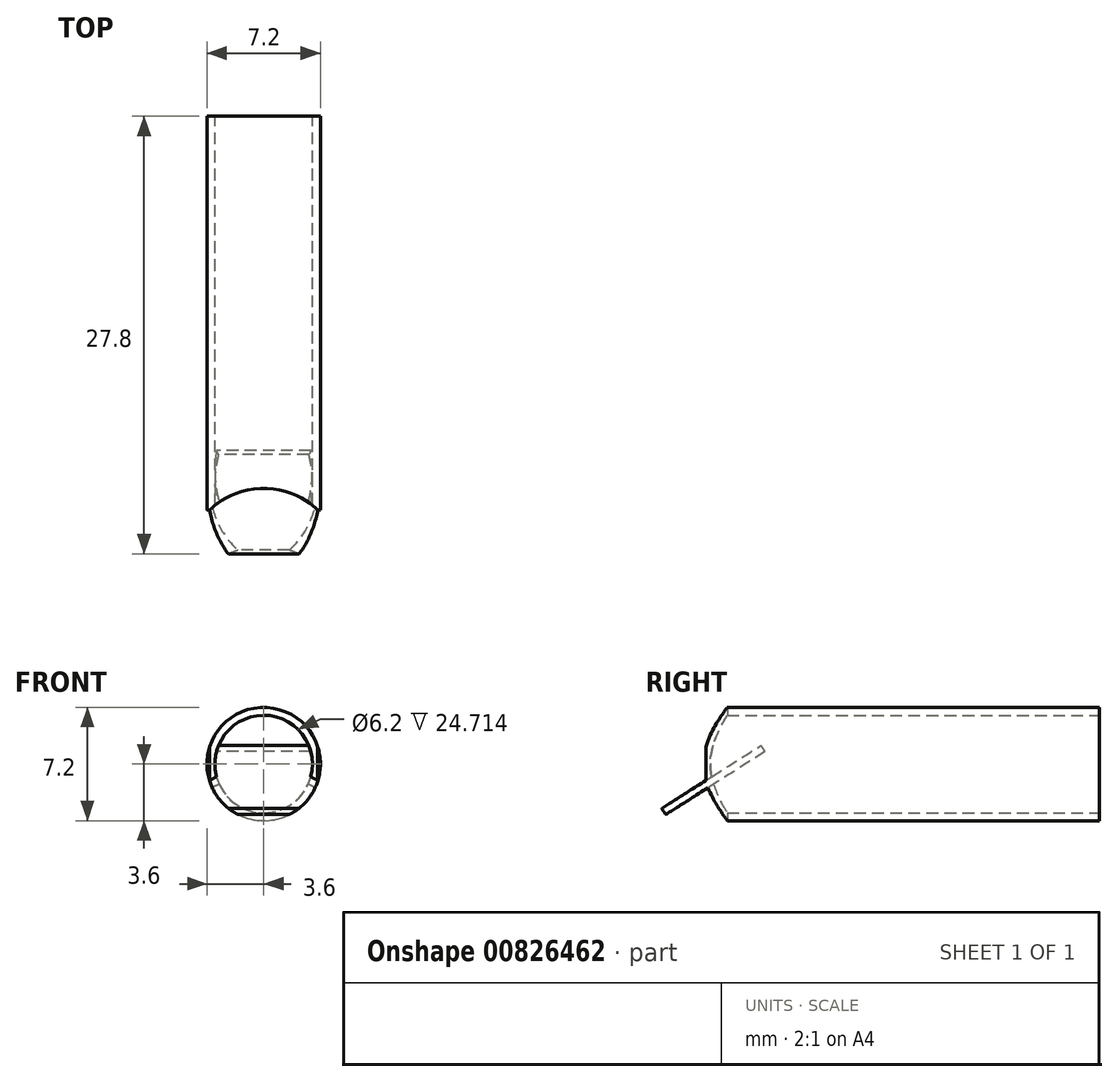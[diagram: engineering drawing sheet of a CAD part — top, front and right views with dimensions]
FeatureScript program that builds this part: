
annotation { "Feature Type Name" : "Feature", "Feature Type Description" : "" }
export const myFeature = defineFeature(function(context is Context, id is Id, definition is map)
    precondition{}
    {
        {
            var Q0;
            Q0=qCreatedBy(makeId("Front.planeOp"),FACE);
            var sketch = newSketch(context, id + "F0", { "sketchPlane" : qUnion([Q0])});
            skCircle(sketch, "E0", {"center": v(0, 0) * mm, "radius": 3.1 * mm});
            skCircle(sketch, "E1", {"center": v(0, 0) * mm, "radius": 3.6 * mm});
            skSolve(sketch);
        }
        {
            var Q0;
            Q0 = qSketchRegion(id + "F0", true);
            extrude(context, id + "F1", {"entities" : qUnion([Q0]), "endBound" : BoundingType.SYMMETRIC, "depth" : 25 * mm, "offsetDistance" : 25 * mm});
        }
        {
            var Q0;
            Q0=qCreatedBy(makeId("Top.planeOp"),FACE);
            var sketch = newSketch(context, id + "F2", { "sketchPlane" : qUnion([Q0])});
            skCircle(sketch, "E2", {"center": v(0, -16.14) * mm, "radius": 5 * mm});
            skSolve(sketch);
        }
        {
            var Q0;
            Q0 = qSketchRegion(id + "F2", true);
            extrude(context, id + "F3", {"entities" : qUnion([Q0]), "operationType" : NewBodyOperationType.REMOVE, "endBound" : BoundingType.SYMMETRIC, "depth" : 25 * mm, "offsetDistance" : 25 * mm});
        }
        {
            var Q0;
            Q0=qCreatedBy(makeId("Right.planeOp"),FACE);
            var sketch = newSketch(context, id + "F4", { "sketchPlane" : qUnion([Q0])});
            skLineSegment(sketch, "E3.bottom", {"start": v(-15.05, -3.2) * mm, "end": v(-8.74, 0.8) * mm});
            skLineSegment(sketch, "E3.top", {"start": v(-15.3, -2.82) * mm, "end": v(-8.98, 1.18) * mm});
            skLineSegment(sketch, "E3.left", {"start": v(-15.05, -3.2) * mm, "end": v(-15.3, -2.82) * mm});
            skLineSegment(sketch, "E3.right", {"start": v(-8.74, 0.8) * mm, "end": v(-8.98, 1.18) * mm});
            skSolve(sketch);
        }
        {
            var Q0;
            Q0 = qSketchRegion(id + "F4", true);
            var Q1;
            Q1 = qSketchRegion(id + "F6", true);
            extrude(context, id + "F5", {"entities" : qUnion([Q0, Q1]), "operationType" : NewBodyOperationType.ADD, "endBound" : BoundingType.SYMMETRIC, "depth" : 8 * mm, "offsetDistance" : 25 * mm});
        }
        {
            var Q0;
            Q0=qCreatedBy(makeId("Front.planeOp"),FACE);
            var sketch = newSketch(context, id + "F6", { "sketchPlane" : qUnion([Q0])});
            skCircle(sketch, "E4", {"center": v(0, 0) * mm, "radius": 3.6 * mm});
            skCircle(sketch, "E5", {"center": v(0, 0) * mm, "radius": 5.68 * mm});
            skSolve(sketch);
        }
        {
            var Q0;
            Q0 = qSketchRegion(id + "F6", true);
            extrude(context, id + "F7", {"entities" : qUnion([Q0]), "operationType" : NewBodyOperationType.REMOVE, "endBound" : BoundingType.SYMMETRIC, "oppositeDirection" : true, "depth" : 50 * mm, "offsetDistance" : 25 * mm});
        }
    });
